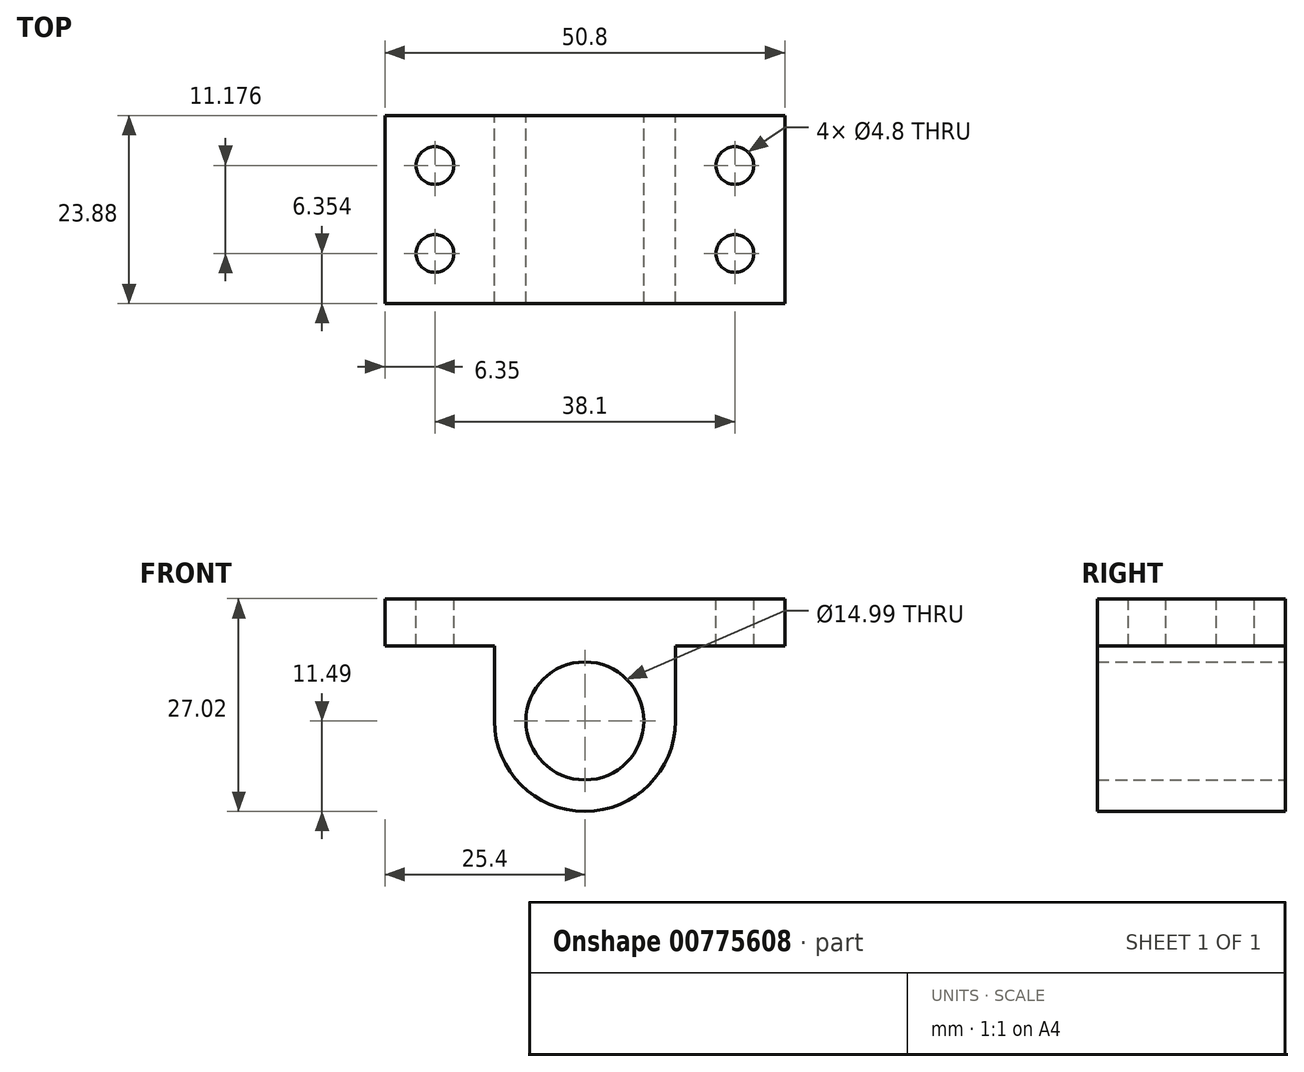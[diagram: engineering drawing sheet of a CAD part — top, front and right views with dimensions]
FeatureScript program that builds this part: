
annotation { "Feature Type Name" : "Feature", "Feature Type Description" : "" }
export const myFeature = defineFeature(function(context is Context, id is Id, definition is map)
    precondition{}
    {
        {
            var Q0;
            Q0=qCreatedBy(makeId("Front.planeOp"),FACE);
            var sketch = newSketch(context, id + "F0", { "sketchPlane" : qUnion([Q0])});
            skCircle(sketch, "E0", {"center": v(0, 0) * mm, "radius": 7.5 * mm});
            skLineSegment(sketch, "E1", {"start": v(-25.4, 15.52) * mm, "end": v(-25.4, 9.52) * mm});
            skLineSegment(sketch, "E2", {"start": v(-25.4, 9.52) * mm, "end": v(-11.5, 9.52) * mm});
            skLineSegment(sketch, "E3", {"start": v(-25.4, 15.52) * mm, "end": v(25.4, 15.52) * mm});
            skLineSegment(sketch, "E4", {"start": v(25.4, 15.52) * mm, "end": v(25.4, 9.52) * mm});
            skLineSegment(sketch, "E5", {"start": v(25.4, 9.52) * mm, "end": v(11.5, 9.52) * mm});
            skArc(sketch, "E6", {"start": v(-11.5, 0) * mm, "mid": v(0, -11.5) * mm, "end": v(11.5, 0) * mm});
            skLineSegment(sketch, "E7", {"start": v(-11.5, 0) * mm, "end": v(-11.5, 9.52) * mm});
            skLineSegment(sketch, "E8", {"start": v(11.5, 9.52) * mm, "end": v(11.5, 0) * mm});
            skSolve(sketch);
        }
        {
            var Q0;
            Q0 = qSketchRegion(id + "F0", true);
            extrude(context, id + "F1", {"entities" : qUnion([Q0]), "depth" : 23.88 * mm, "offsetDistance" : 25.4 * mm});
        }
        {
            var Q0;
            Q0=makeQuery(id+"F1.opExtrude","SWEPT_FACE",FACE,{"disambiguationData":[OSD([sQuery(id+"F0.wireOp",EDGE,"E3")])]});
            var sketch = newSketch(context, id + "F2", { "sketchPlane" : qUnion([Q0])});
            skCircle(sketch, "E9", {"center": v(-19.05, -6.35) * mm, "radius": 2.4 * mm});
            skCircle(sketch, "E10", {"center": v(-19.05, -17.53) * mm, "radius": 2.4 * mm});
            skCircle(sketch, "E11", {"center": v(19.05, -17.53) * mm, "radius": 2.4 * mm});
            skCircle(sketch, "E12", {"center": v(19.05, -6.35) * mm, "radius": 2.4 * mm});
            skSolve(sketch);
        }
        {
            var Q0;
            Q0 = qSketchRegion(id + "F2", true);
            extrude(context, id + "F3", {"entities" : qUnion([Q0]), "operationType" : NewBodyOperationType.REMOVE, "endBound" : BoundingType.UP_TO_NEXT, "oppositeDirection" : true, "depth" : 25.4 * mm, "offsetDistance" : 25.4 * mm});
        }
    });
